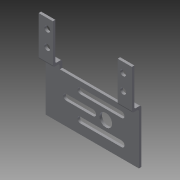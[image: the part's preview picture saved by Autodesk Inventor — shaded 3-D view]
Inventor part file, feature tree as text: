
AUTODESK INVENTOR PART (.ipt)
format: ipt  version: 2014 (Build 180170000, 170)  size: 152,064 bytes
history: native  units: in
note: dims shown in document units (in); Inventor stores cm internally (conversion verified against a paired STEP export)
features: extrude x4, sketch x4, projected_geometry x1
ambient origin geometry x8: Origin, YZ Plane, XZ Plane, XY Plane, X Axis, Y Axis, Z Axis, Center Point
bodies: Solid1 (feature_tree)
feature tree (9):
  extrude  "Extrusion1"  Depth=0.0625in
  extrude  "Extrusion2"  Depth=1.0in
  extrude  "Extrusion3"  Depth=0.05in
  extrude  "Extrusion4"  Depth=0.3543in
  sketch  "Sketch1"  dims[d0=1.3386in d1=0.0625in]
  sketch  "Sketch2"  dims[d3=0.0625in d4=1.0in]
  sketch  "Sketch3"  dims[d5=0.0625in d7=0.05in]
  sketch  "Sketch4"  dims[d8=2.3228in d9=0.0in d10=0.3543in d11=0.3543in d12=1.122in d13=0.0in d21=0.6693in d22=0.147in d23=1.122in d24=0.0in d39=1.122in d40=0.0in]
  projected_geometry  "Projected Loop1"
